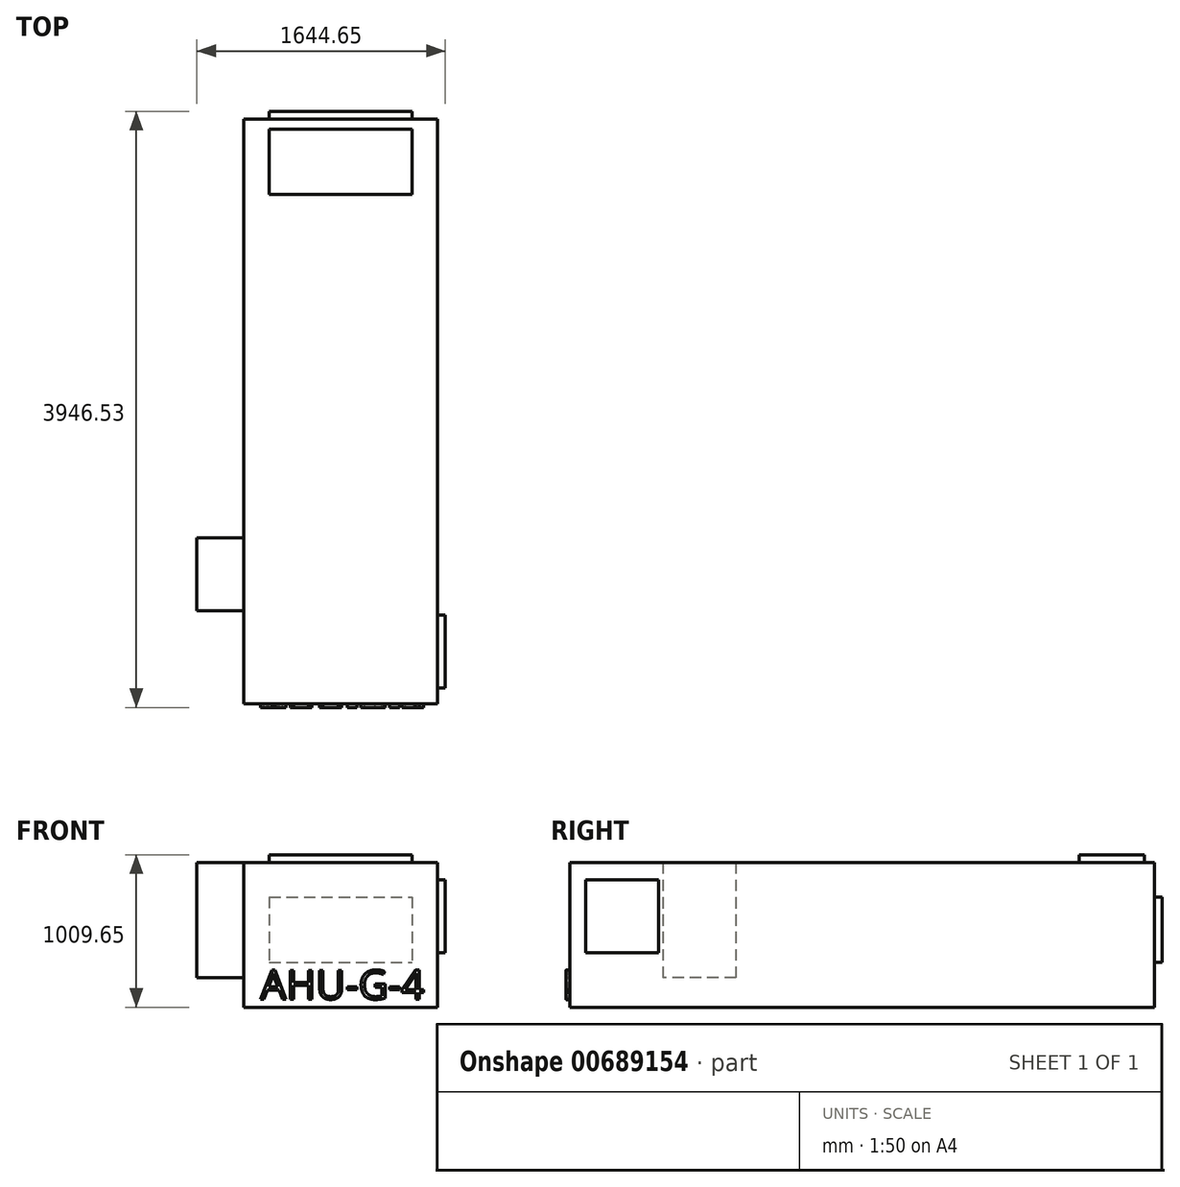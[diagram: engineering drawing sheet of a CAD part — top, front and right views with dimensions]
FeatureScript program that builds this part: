
annotation { "Feature Type Name" : "Feature", "Feature Type Description" : "" }
export const myFeature = defineFeature(function(context is Context, id is Id, definition is map)
    precondition{}
    {
        {
            var Q0;
            Q0=qCreatedBy(makeId("Front.planeOp"),FACE);
            var sketch = newSketch(context, id + "F0", { "sketchPlane" : qUnion([Q0])});
            skLineSegment(sketch, "E0.bottom", {"start": v(-639.94, 406.41) * mm, "end": v(642.76, 406.41) * mm});
            skLineSegment(sketch, "E0.top", {"start": v(-639.94, -552.44) * mm, "end": v(642.76, -552.44) * mm});
            skLineSegment(sketch, "E0.left", {"start": v(-639.94, 406.41) * mm, "end": v(-639.94, -552.44) * mm});
            skLineSegment(sketch, "E0.right", {"start": v(642.76, 406.41) * mm, "end": v(642.76, -552.44) * mm});
            skSolve(sketch);
        }
        {
            var Q0;
            Q0=qSketchRegion(id+"F0",true);
            extrude(context, id + "F1", {"entities" : qUnion([Q0]), "depth" : 3870.32 * mm, "offsetDistance" : 25.4 * mm});
        }
        {
            var Q0;
            Q0=makeQuery(id+"F1.opExtrude","SWEPT_FACE",FACE,{"disambiguationData":[OSD([sQuery(id+"F0.wireOp",EDGE,"E0.right")])]});
            var sketch = newSketch(context, id + "F2", { "sketchPlane" : qUnion([Q0])});
            skLineSegment(sketch, "E1.bottom", {"start": v(-3765.55, 292.11) * mm, "end": v(-3282.95, 292.11) * mm});
            skLineSegment(sketch, "E1.top", {"start": v(-3765.55, -190.49) * mm, "end": v(-3282.95, -190.49) * mm});
            skLineSegment(sketch, "E1.left", {"start": v(-3765.55, 292.11) * mm, "end": v(-3765.55, -190.49) * mm});
            skLineSegment(sketch, "E1.right", {"start": v(-3282.95, 292.11) * mm, "end": v(-3282.95, -190.49) * mm});
            skSolve(sketch);
        }
        {
            var Q0;
            Q0 = qSketchRegion(id + "F2", true);
            extrude(context, id + "F3", {"entities" : qUnion([Q0]), "operationType" : NewBodyOperationType.ADD, "depth" : 50.8 * mm, "offsetDistance" : 25.4 * mm});
        }
        {
            var Q0;
            Q0=makeQuery(id+"F1.opExtrude","SWEPT_FACE",FACE,{"disambiguationData":[OSD([sQuery(id+"F0.wireOp",EDGE,"E0.left")])]});
            var sketch = newSketch(context, id + "F4", { "sketchPlane" : qUnion([Q0])});
            skLineSegment(sketch, "E2.bottom", {"start": v(2771.78, 406.41) * mm, "end": v(3254.38, 406.41) * mm});
            skLineSegment(sketch, "E2.top", {"start": v(2771.78, -355.59) * mm, "end": v(3254.38, -355.59) * mm});
            skLineSegment(sketch, "E2.left", {"start": v(2771.78, 406.41) * mm, "end": v(2771.78, -355.59) * mm});
            skLineSegment(sketch, "E2.right", {"start": v(3254.38, 406.41) * mm, "end": v(3254.38, -355.59) * mm});
            skSolve(sketch);
        }
        {
            var Q0;
            Q0 = qSketchRegion(id + "F4", true);
            extrude(context, id + "F5", {"entities" : qUnion([Q0]), "depth" : 311.15 * mm, "offsetDistance" : 25.4 * mm});
        }
        {
            var Q0;
            Q0=makeQuery(id+"F1.opExtrude","CAP_FACE",FACE,{"disambiguationData":[OSD([sQuery(id+"F0.wireOp",EDGE,"E0.bottom"),sQuery(id+"F0.wireOp",EDGE,"E0.top"),sQuery(id+"F0.wireOp",EDGE,"E0.left"),sQuery(id+"F0.wireOp",EDGE,"E0.right")])],"isStart":false});
            var sketch = newSketch(context, id + "F6", { "sketchPlane" : qUnion([Q0])});
            skText(sketch, "E3", { "text": "AHU-G-4", "fontName": "OpenSans-Regular.ttf"});
            const initialGuessF6  = {"E3": [-0.52978, -0.49919, 1, 0, 0.19308]};
            skSetInitialGuess(sketch, initialGuessF6);
            skSolve(sketch);
        }
        {
            var Q0;
            Q0 = qSketchRegion(id + "F6", true);
            extrude(context, id + "F7", {"entities" : qUnion([Q0]), "operationType" : NewBodyOperationType.ADD, "depth" : 25.4 * mm, "offsetDistance" : 25.4 * mm});
        }
        {
            var Q0;
            Q0=makeQuery(id+"F1.opExtrude","SWEPT_FACE",FACE,{"disambiguationData":[OSD([sQuery(id+"F0.wireOp",EDGE,"E0.bottom")])]});
            var sketch = newSketch(context, id + "F8", { "sketchPlane" : qUnion([Q0])});
            skLineSegment(sketch, "E4.bottom", {"start": v(-471.67, -498.48) * mm, "end": v(474.48, -498.47) * mm});
            skLineSegment(sketch, "E4.top", {"start": v(-471.67, -66.68) * mm, "end": v(474.48, -66.67) * mm});
            skLineSegment(sketch, "E4.left", {"start": v(-471.67, -498.48) * mm, "end": v(-471.67, -66.68) * mm});
            skLineSegment(sketch, "E4.right", {"start": v(474.48, -498.47) * mm, "end": v(474.48, -66.67) * mm});
            skSolve(sketch);
        }
        {
            var Q0;
            Q0 = qSketchRegion(id + "F8", true);
            extrude(context, id + "F9", {"entities" : qUnion([Q0]), "operationType" : NewBodyOperationType.ADD, "depth" : 50.8 * mm, "offsetDistance" : 25.4 * mm});
        }
        {
            var Q0;
            Q0=makeQuery(id+"F1.opExtrude","CAP_FACE",FACE,{"disambiguationData":[OSD([sQuery(id+"F0.wireOp",EDGE,"E0.bottom"),sQuery(id+"F0.wireOp",EDGE,"E0.top"),sQuery(id+"F0.wireOp",EDGE,"E0.left"),sQuery(id+"F0.wireOp",EDGE,"E0.right")])],"isStart":true});
            var sketch = newSketch(context, id + "F10", { "sketchPlane" : qUnion([Q0])});
            skLineSegment(sketch, "E5.bottom", {"start": v(471.67, 177.81) * mm, "end": v(-474.48, 177.81) * mm});
            skLineSegment(sketch, "E5.top", {"start": v(471.67, -253.99) * mm, "end": v(-474.48, -253.99) * mm});
            skLineSegment(sketch, "E5.left", {"start": v(471.67, 177.81) * mm, "end": v(471.67, -253.99) * mm});
            skLineSegment(sketch, "E5.right", {"start": v(-474.48, 177.81) * mm, "end": v(-474.48, -253.99) * mm});
            skSolve(sketch);
        }
        {
            var Q0;
            Q0 = qSketchRegion(id + "F10", true);
            extrude(context, id + "F11", {"entities" : qUnion([Q0]), "operationType" : NewBodyOperationType.ADD, "depth" : 50.8 * mm, "offsetDistance" : 25.4 * mm});
        }
    });
